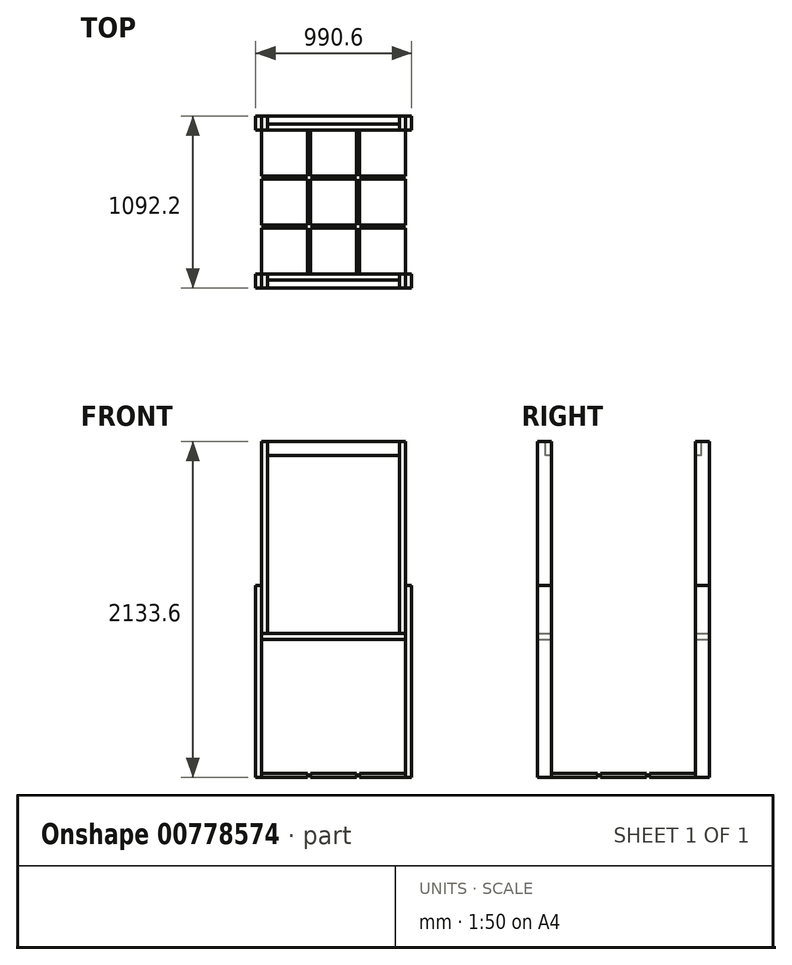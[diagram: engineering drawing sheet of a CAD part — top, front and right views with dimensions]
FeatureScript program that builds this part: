
annotation { "Feature Type Name" : "Feature", "Feature Type Description" : "" }
export const myFeature = defineFeature(function(context is Context, id is Id, definition is map)
    precondition{}
    {
        {
            var Q0;
            Q0=qCreatedBy(makeId("Top.planeOp"),FACE);
            var sketch = newSketch(context, id + "F0", { "sketchPlane" : qUnion([Q0])});
            skLineSegment(sketch, "E0.bottom", {"start": v(457.2, 457.2) * mm, "end": v(-457.2, 457.2) * mm, "construction": true});
            skLineSegment(sketch, "E0.top", {"start": v(457.2, -457.2) * mm, "end": v(-457.2, -457.2) * mm, "construction": true});
            skLineSegment(sketch, "E0.left", {"start": v(457.2, 457.2) * mm, "end": v(457.2, -457.2) * mm, "construction": true});
            skLineSegment(sketch, "E0.right", {"start": v(-457.2, 457.2) * mm, "end": v(-457.2, -457.2) * mm, "construction": true});
            skPoint(sketch, "E0.middle", {"position": v(0, 0) * mm});
            skLineSegment(sketch, "E1.bottom", {"start": v(-457.2, 457.2) * mm, "end": v(-165.1, 457.2) * mm});
            skLineSegment(sketch, "E1.top", {"start": v(-457.2, 165.1) * mm, "end": v(-165.1, 165.1) * mm});
            skLineSegment(sketch, "E1.left", {"start": v(-457.2, 457.2) * mm, "end": v(-457.2, 165.1) * mm});
            skLineSegment(sketch, "E1.right", {"start": v(-165.1, 457.2) * mm, "end": v(-165.1, 165.1) * mm});
            skLineSegment(sketch, "E2.0.1.0", {"start": v(-165.1, 146.05) * mm, "end": v(-165.1, -146.05) * mm});
            skLineSegment(sketch, "E2.0.1.1", {"start": v(-457.2, 146.05) * mm, "end": v(-457.2, -146.05) * mm});
            skLineSegment(sketch, "E2.0.1.2", {"start": v(-457.2, -146.05) * mm, "end": v(-165.1, -146.05) * mm});
            skLineSegment(sketch, "E2.0.1.3", {"start": v(-457.2, 146.05) * mm, "end": v(-165.1, 146.05) * mm});
            skLineSegment(sketch, "E2.0.2.0", {"start": v(-165.1, -165.1) * mm, "end": v(-165.1, -457.2) * mm});
            skLineSegment(sketch, "E2.0.2.1", {"start": v(-457.2, -165.1) * mm, "end": v(-457.2, -457.2) * mm});
            skLineSegment(sketch, "E2.0.2.2", {"start": v(-457.2, -457.2) * mm, "end": v(-165.1, -457.2) * mm});
            skLineSegment(sketch, "E2.0.2.3", {"start": v(-457.2, -165.1) * mm, "end": v(-165.1, -165.1) * mm});
            skLineSegment(sketch, "E2.1.0.0", {"start": v(146.05, 457.2) * mm, "end": v(146.05, 165.1) * mm});
            skLineSegment(sketch, "E2.1.0.1", {"start": v(-146.05, 457.2) * mm, "end": v(-146.05, 165.1) * mm});
            skLineSegment(sketch, "E2.1.0.2", {"start": v(-146.05, 165.1) * mm, "end": v(146.05, 165.1) * mm});
            skLineSegment(sketch, "E2.1.0.3", {"start": v(-146.05, 457.2) * mm, "end": v(146.05, 457.2) * mm});
            skLineSegment(sketch, "E2.1.1.0", {"start": v(146.05, 146.05) * mm, "end": v(146.05, -146.05) * mm});
            skLineSegment(sketch, "E2.1.1.1", {"start": v(-146.05, 146.05) * mm, "end": v(-146.05, -146.05) * mm});
            skLineSegment(sketch, "E2.1.1.2", {"start": v(-146.05, -146.05) * mm, "end": v(146.05, -146.05) * mm});
            skLineSegment(sketch, "E2.1.1.3", {"start": v(-146.05, 146.05) * mm, "end": v(146.05, 146.05) * mm});
            skLineSegment(sketch, "E2.1.2.0", {"start": v(146.05, -165.1) * mm, "end": v(146.05, -457.2) * mm});
            skLineSegment(sketch, "E2.1.2.1", {"start": v(-146.05, -165.1) * mm, "end": v(-146.05, -457.2) * mm});
            skLineSegment(sketch, "E2.1.2.2", {"start": v(-146.05, -457.2) * mm, "end": v(146.05, -457.2) * mm});
            skLineSegment(sketch, "E2.1.2.3", {"start": v(-146.05, -165.1) * mm, "end": v(146.05, -165.1) * mm});
            skLineSegment(sketch, "E2.2.0.0", {"start": v(457.2, 457.2) * mm, "end": v(457.2, 165.1) * mm});
            skLineSegment(sketch, "E2.2.0.1", {"start": v(165.1, 457.2) * mm, "end": v(165.1, 165.1) * mm});
            skLineSegment(sketch, "E2.2.0.2", {"start": v(165.1, 165.1) * mm, "end": v(457.2, 165.1) * mm});
            skLineSegment(sketch, "E2.2.0.3", {"start": v(165.1, 457.2) * mm, "end": v(457.2, 457.2) * mm});
            skLineSegment(sketch, "E2.2.1.0", {"start": v(457.2, 146.05) * mm, "end": v(457.2, -146.05) * mm});
            skLineSegment(sketch, "E2.2.1.1", {"start": v(165.1, 146.05) * mm, "end": v(165.1, -146.05) * mm});
            skLineSegment(sketch, "E2.2.1.2", {"start": v(165.1, -146.05) * mm, "end": v(457.2, -146.05) * mm});
            skLineSegment(sketch, "E2.2.1.3", {"start": v(165.1, 146.05) * mm, "end": v(457.2, 146.05) * mm});
            skLineSegment(sketch, "E2.2.2.0", {"start": v(457.2, -165.1) * mm, "end": v(457.2, -457.2) * mm});
            skLineSegment(sketch, "E2.2.2.1", {"start": v(165.1, -165.1) * mm, "end": v(165.1, -457.2) * mm});
            skLineSegment(sketch, "E2.2.2.2", {"start": v(165.1, -457.2) * mm, "end": v(457.2, -457.2) * mm});
            skLineSegment(sketch, "E2.2.2.3", {"start": v(165.1, -165.1) * mm, "end": v(457.2, -165.1) * mm});
            skLineSegment(sketch, "E2.direction1", {"start": v(-457.2, 165.1) * mm, "end": v(-146.05, 165.1) * mm, "construction": true});
            skLineSegment(sketch, "E2.direction2", {"start": v(-457.2, 165.1) * mm, "end": v(-457.2, -146.05) * mm, "construction": true});
            skSolve(sketch);
        }
        {
            var Q0;
            Q0 = qSketchRegion(id + "F0", true);
            extrude(context, id + "F1", {"entities" : qUnion([Q0]), "depth" : 25.4 * mm, "offsetDistance" : 25.4 * mm});
        }
        {
            var Q0;
            Q0=qCreatedBy(makeId("Top.planeOp"),FACE);
            var sketch = newSketch(context, id + "F2", { "sketchPlane" : qUnion([Q0])});
            skLineSegment(sketch, "E3.bottom", {"start": v(-495.3, 546.1) * mm, "end": v(-457.2, 546.1) * mm});
            skLineSegment(sketch, "E3.top", {"start": v(-495.3, 457.2) * mm, "end": v(-457.2, 457.2) * mm});
            skLineSegment(sketch, "E3.left", {"start": v(-495.3, 546.1) * mm, "end": v(-495.3, 457.2) * mm});
            skLineSegment(sketch, "E3.right", {"start": v(-457.2, 546.1) * mm, "end": v(-457.2, 457.2) * mm});
            skLineSegment(sketch, "E4.0.1.0", {"start": v(-495.3, -457.2) * mm, "end": v(-457.2, -457.2) * mm});
            skLineSegment(sketch, "E4.0.1.1", {"start": v(-495.3, -546.1) * mm, "end": v(-457.2, -546.1) * mm});
            skLineSegment(sketch, "E4.0.1.2", {"start": v(-495.3, -457.2) * mm, "end": v(-495.3, -546.1) * mm});
            skLineSegment(sketch, "E4.0.1.3", {"start": v(-457.2, -457.2) * mm, "end": v(-457.2, -546.1) * mm});
            skLineSegment(sketch, "E4.1.0.0", {"start": v(457.2, 546.1) * mm, "end": v(495.3, 546.1) * mm});
            skLineSegment(sketch, "E4.1.0.1", {"start": v(457.2, 457.2) * mm, "end": v(495.3, 457.2) * mm});
            skLineSegment(sketch, "E4.1.0.2", {"start": v(457.2, 546.1) * mm, "end": v(457.2, 457.2) * mm});
            skLineSegment(sketch, "E4.1.0.3", {"start": v(495.3, 546.1) * mm, "end": v(495.3, 457.2) * mm});
            skLineSegment(sketch, "E4.1.1.0", {"start": v(457.2, -457.2) * mm, "end": v(495.3, -457.2) * mm});
            skLineSegment(sketch, "E4.1.1.1", {"start": v(457.2, -546.1) * mm, "end": v(495.3, -546.1) * mm});
            skLineSegment(sketch, "E4.1.1.2", {"start": v(457.2, -457.2) * mm, "end": v(457.2, -546.1) * mm});
            skLineSegment(sketch, "E4.1.1.3", {"start": v(495.3, -457.2) * mm, "end": v(495.3, -546.1) * mm});
            skLineSegment(sketch, "E4.direction1", {"start": v(-495.3, 457.2) * mm, "end": v(457.2, 457.2) * mm, "construction": true});
            skLineSegment(sketch, "E4.direction2", {"start": v(-495.3, 457.2) * mm, "end": v(-495.3, -546.1) * mm, "construction": true});
            skSolve(sketch);
        }
        {
            var Q0;
            Q0 = qSketchRegion(id + "F2", true);
            extrude(context, id + "F3", {"entities" : qUnion([Q0]), "depth" : 1219.2 * mm, "offsetDistance" : 25.4 * mm});
        }
        {
            var Q0;
            Q0=makeQuery(id+"F3.opExtrude","CAP_FACE",FACE,{"disambiguationData":[OSD([sQuery(id+"F2.wireOp",EDGE,"E4.0.1.0"),sQuery(id+"F2.wireOp",EDGE,"E4.0.1.1"),sQuery(id+"F2.wireOp",EDGE,"E4.0.1.2"),sQuery(id+"F2.wireOp",EDGE,"E4.0.1.3")])],"isStart":false});
            cPlane(context, id + "F4", {"entities" : qUnion([Q0]), "cplaneType" : CPlaneType.OFFSET, "offset" : 304.8 * mm, "oppositeDirection" : true, "width" : 152.4 * mm, "height" : 152.4 * mm});
        }
        {
            var Q0;
            Q0=qCreatedBy(id+"F4.planeOp",FACE);
            var sketch = newSketch(context, id + "F5", { "sketchPlane" : qUnion([Q0])});
            skLineSegment(sketch, "E5.bottom", {"start": v(-457.2, 457.2) * mm, "end": v(-419.1, 457.2) * mm});
            skLineSegment(sketch, "E5.top", {"start": v(-457.2, 546.1) * mm, "end": v(-419.1, 546.1) * mm});
            skLineSegment(sketch, "E5.left", {"start": v(-457.2, 457.2) * mm, "end": v(-457.2, 546.1) * mm});
            skLineSegment(sketch, "E5.right", {"start": v(-419.1, 457.2) * mm, "end": v(-419.1, 546.1) * mm});
            skLineSegment(sketch, "E6.0.1.0", {"start": v(-457.2, -546.1) * mm, "end": v(-457.2, -457.2) * mm});
            skLineSegment(sketch, "E6.0.1.1", {"start": v(-419.1, -546.1) * mm, "end": v(-419.1, -457.2) * mm});
            skLineSegment(sketch, "E6.0.1.2", {"start": v(-457.2, -546.1) * mm, "end": v(-419.1, -546.1) * mm});
            skLineSegment(sketch, "E6.0.1.3", {"start": v(-457.2, -457.2) * mm, "end": v(-419.1, -457.2) * mm});
            skLineSegment(sketch, "E6.1.0.0", {"start": v(419.1, 457.2) * mm, "end": v(419.1, 546.1) * mm});
            skLineSegment(sketch, "E6.1.0.1", {"start": v(457.2, 457.2) * mm, "end": v(457.2, 546.1) * mm});
            skLineSegment(sketch, "E6.1.0.2", {"start": v(419.1, 457.2) * mm, "end": v(457.2, 457.2) * mm});
            skLineSegment(sketch, "E6.1.0.3", {"start": v(419.1, 546.1) * mm, "end": v(457.2, 546.1) * mm});
            skLineSegment(sketch, "E6.1.1.0", {"start": v(419.1, -546.1) * mm, "end": v(419.1, -457.2) * mm});
            skLineSegment(sketch, "E6.1.1.1", {"start": v(457.2, -546.1) * mm, "end": v(457.2, -457.2) * mm});
            skLineSegment(sketch, "E6.1.1.2", {"start": v(419.1, -546.1) * mm, "end": v(457.2, -546.1) * mm});
            skLineSegment(sketch, "E6.1.1.3", {"start": v(419.1, -457.2) * mm, "end": v(457.2, -457.2) * mm});
            skLineSegment(sketch, "E6.direction1", {"start": v(-457.2, 457.2) * mm, "end": v(419.1, 457.2) * mm, "construction": true});
            skLineSegment(sketch, "E6.direction2", {"start": v(-457.2, 457.2) * mm, "end": v(-457.2, -546.1) * mm, "construction": true});
            skSolve(sketch);
        }
        {
            var Q0;
            Q0 = qSketchRegion(id + "F5", true);
            extrude(context, id + "F6", {"entities" : qUnion([Q0]), "depth" : 1219.2 * mm, "offsetDistance" : 25.4 * mm});
        }
        {
            var Q0;
            Q0=makeQuery(id+"F3.opExtrude","SWEPT_FACE",FACE,{"disambiguationData":[OSD([sQuery(id+"F2.wireOp",EDGE,"E4.0.1.3")])]});
            var sketch = newSketch(context, id + "F7", { "sketchPlane" : qUnion([Q0])});
            skLineSegment(sketch, "E7.bottom", {"start": v(-546.1, 914.4) * mm, "end": v(-457.2, 914.4) * mm});
            skLineSegment(sketch, "E7.top", {"start": v(-546.1, 876.3) * mm, "end": v(-457.2, 876.3) * mm});
            skLineSegment(sketch, "E7.left", {"start": v(-546.1, 914.4) * mm, "end": v(-546.1, 876.3) * mm});
            skLineSegment(sketch, "E7.right", {"start": v(-457.2, 914.4) * mm, "end": v(-457.2, 876.3) * mm});
            skLineSegment(sketch, "E8.1.0.0", {"start": v(457.2, 914.4) * mm, "end": v(546.1, 914.4) * mm});
            skLineSegment(sketch, "E8.1.0.1", {"start": v(546.1, 914.4) * mm, "end": v(546.1, 876.3) * mm});
            skLineSegment(sketch, "E8.1.0.2", {"start": v(457.2, 914.4) * mm, "end": v(457.2, 876.3) * mm});
            skLineSegment(sketch, "E8.1.0.3", {"start": v(457.2, 876.3) * mm, "end": v(546.1, 876.3) * mm});
            skLineSegment(sketch, "E8.direction1", {"start": v(-546.1, 876.3) * mm, "end": v(457.2, 876.3) * mm, "construction": true});
            skSolve(sketch);
        }
        {
            var Q0;
            Q0 = qSketchRegion(id + "F7", true);
            var Q1;
            Q1=makeQuery(id+"F3.opExtrude","SWEPT_FACE",FACE,{"disambiguationData":[OSD([sQuery(id+"F2.wireOp",EDGE,"E4.1.0.2")])]});
            extrude(context, id + "F8", {"entities" : qUnion([Q0]), "endBound" : BoundingType.UP_TO_SURFACE, "depth" : 25.4 * mm, "endBoundEntityFace" : qUnion([Q1]), "offsetDistance" : 25.4 * mm});
        }
        {
            var Q0;
            Q0=makeQuery(id+"F6.opExtrude","SWEPT_FACE",FACE,{"disambiguationData":[OSD([sQuery(id+"F5.wireOp",EDGE,"E6.0.1.1")])]});
            var sketch = newSketch(context, id + "F9", { "sketchPlane" : qUnion([Q0])});
            skLineSegment(sketch, "E9.bottom", {"start": v(-495.3, 2133.6) * mm, "end": v(-457.2, 2133.6) * mm});
            skLineSegment(sketch, "E9.top", {"start": v(-495.3, 2044.7) * mm, "end": v(-457.2, 2044.7) * mm});
            skLineSegment(sketch, "E9.left", {"start": v(-495.3, 2133.6) * mm, "end": v(-495.3, 2044.7) * mm});
            skLineSegment(sketch, "E9.right", {"start": v(-457.2, 2133.6) * mm, "end": v(-457.2, 2044.7) * mm});
            skLineSegment(sketch, "E10.1.0.0", {"start": v(457.2, 2133.6) * mm, "end": v(495.3, 2133.6) * mm});
            skLineSegment(sketch, "E10.1.0.1", {"start": v(457.2, 2044.7) * mm, "end": v(495.3, 2044.7) * mm});
            skLineSegment(sketch, "E10.1.0.2", {"start": v(457.2, 2133.6) * mm, "end": v(457.2, 2044.7) * mm});
            skLineSegment(sketch, "E10.1.0.3", {"start": v(495.3, 2133.6) * mm, "end": v(495.3, 2044.7) * mm});
            skLineSegment(sketch, "E10.direction1", {"start": v(-495.3, 2044.7) * mm, "end": v(457.2, 2044.7) * mm, "construction": true});
            skSolve(sketch);
        }
        {
            var Q0;
            Q0 = qSketchRegion(id + "F9", true);
            var Q1;
            Q1=makeQuery(id+"F6.opExtrude","SWEPT_FACE",FACE,{"disambiguationData":[OSD([sQuery(id+"F5.wireOp",EDGE,"E6.1.0.0")])]});
            extrude(context, id + "F10", {"entities" : qUnion([Q0]), "endBound" : BoundingType.UP_TO_SURFACE, "depth" : 25.4 * mm, "endBoundEntityFace" : qUnion([Q1]), "offsetDistance" : 25.4 * mm});
        }
    });
